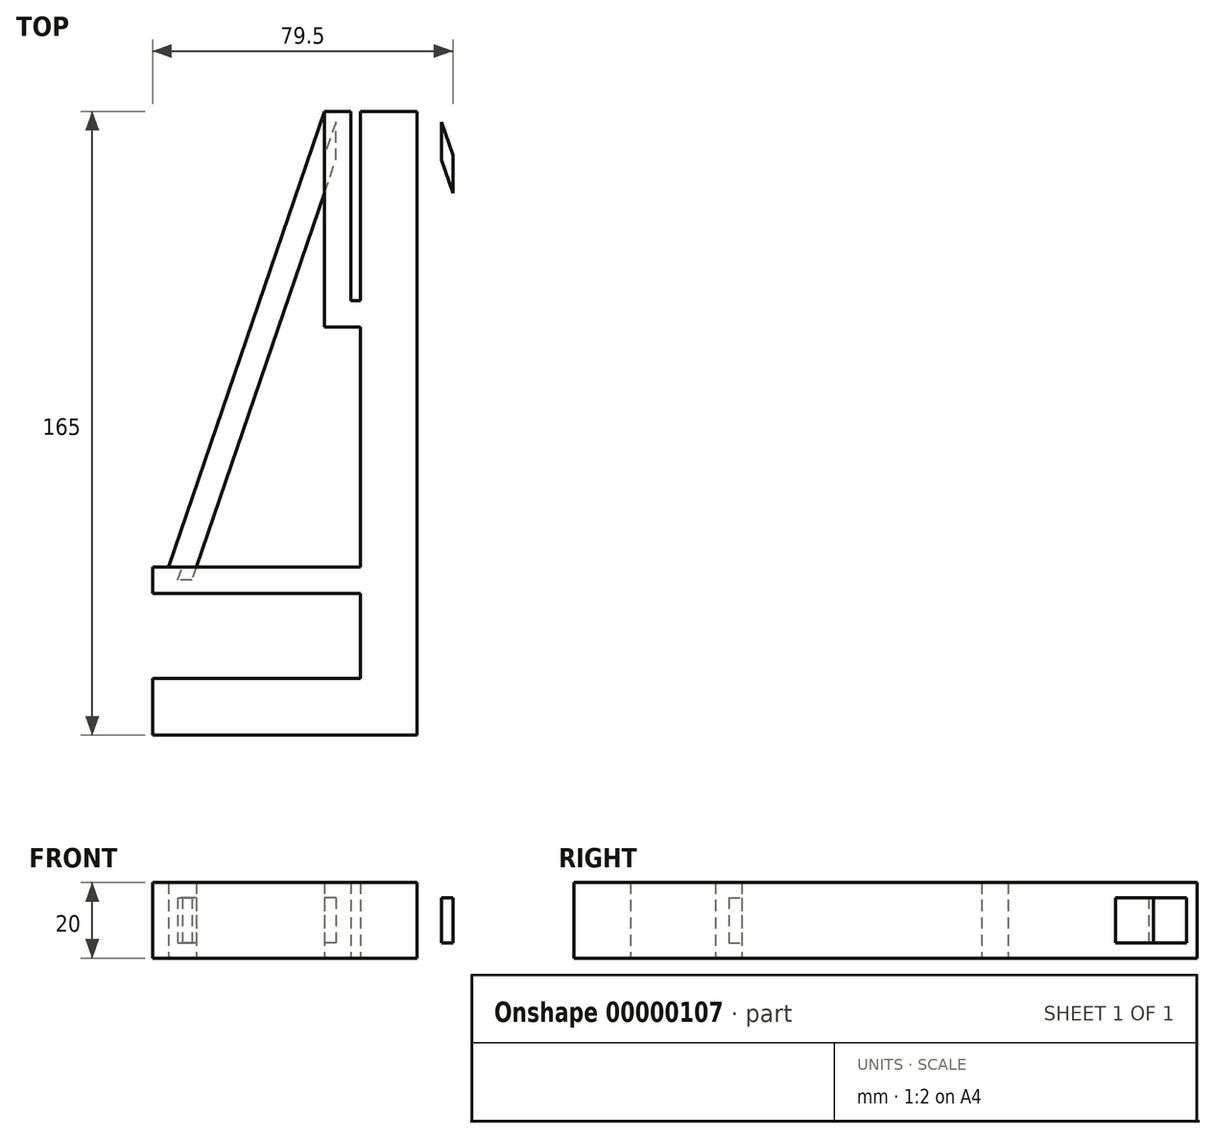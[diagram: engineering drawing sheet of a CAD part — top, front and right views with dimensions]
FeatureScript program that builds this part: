
annotation { "Feature Type Name" : "Feature", "Feature Type Description" : "" }
export const myFeature = defineFeature(function(context is Context, id is Id, definition is map)
    precondition{}
    {
        {
            var Q0;
            Q0=qCreatedBy(makeId("Top.planeOp"),FACE);
            var sketch = newSketch(context, id + "F0", { "sketchPlane" : qUnion([Q0])});
            skLineSegment(sketch, "E0.rect.bottom", {"start": v(7.5, 75) * mm, "end": v(-7.5, 75) * mm});
            skLineSegment(sketch, "E0.rect.left", {"start": v(7.5, 75) * mm, "end": v(7.5, -75) * mm});
            skLineSegment(sketch, "E0.rect.right", {"start": v(-7.5, 75) * mm, "end": v(-7.5, 25) * mm});
            skPoint(sketch, "E0.rect.middle", {"position": v(0, 0) * mm});
            skLineSegment(sketch, "E1.bottom", {"start": v(-7.5, -75) * mm, "end": v(-62.5, -75) * mm});
            skLineSegment(sketch, "E1.top", {"start": v(7.5, -90) * mm, "end": v(-62.5, -90) * mm});
            skLineSegment(sketch, "E1.left", {"start": v(7.5, -75) * mm, "end": v(7.5, -90) * mm});
            skLineSegment(sketch, "E1.right", {"start": v(-62.5, -75) * mm, "end": v(-62.5, -90) * mm});
            skLineSegment(sketch, "E2.bottom", {"start": v(-7.5, -52.5) * mm, "end": v(-62.5, -52.5) * mm});
            skLineSegment(sketch, "E2.top", {"start": v(-7.5, -45.5) * mm, "end": v(-62.5, -45.5) * mm});
            skLineSegment(sketch, "E2.right", {"start": v(-62.5, -52.5) * mm, "end": v(-62.5, -45.5) * mm});
            skLineSegment(sketch, "E3.bottom", {"start": v(-7.5, 18) * mm, "end": v(-17, 18) * mm});
            skLineSegment(sketch, "E3.top", {"start": v(-7.5, 25) * mm, "end": v(-10, 25) * mm});
            skLineSegment(sketch, "E3.right", {"start": v(-17, 18) * mm, "end": v(-17, 25) * mm});
            skLineSegment(sketch, "E4.top", {"start": v(-17, 75) * mm, "end": v(-10, 75) * mm});
            skLineSegment(sketch, "E4.left", {"start": v(-17, 25) * mm, "end": v(-17, 75) * mm});
            skLineSegment(sketch, "E4.right", {"start": v(-10, 25) * mm, "end": v(-10, 75) * mm});
            skLineSegment(sketch, "E5", {"start": v(-17, 75) * mm, "end": v(-58.31, -45.5) * mm, "construction": true});
            skLineSegment(sketch, "E6", {"start": v(-58.31, -45.5) * mm, "end": v(-50.91, -45.5) * mm});
            skLineSegment(sketch, "E7", {"start": v(-50.91, -45.5) * mm, "end": v(-17, 53.42) * mm, "construction": true});
            skLineSegment(sketch, "E8", {"start": v(-17, 53.42) * mm, "end": v(-14, 62.17) * mm, "construction": true});
            skLineSegment(sketch, "E9", {"start": v(-14, 62.17) * mm, "end": v(-14, 72.17) * mm, "construction": true});
            skLineSegment(sketch, "E10", {"start": v(-14, 72.17) * mm, "end": v(-17, 63.42) * mm, "construction": true});
            skLineSegment(sketch, "E11", {"start": v(-50.91, -45.5) * mm, "end": v(-52.11, -49) * mm});
            skLineSegment(sketch, "E12", {"start": v(-52.11, -49) * mm, "end": v(-55.81, -49) * mm});
            skLineSegment(sketch, "E13", {"start": v(-55.81, -49) * mm, "end": v(-54.61, -45.5) * mm});
            skLineSegment(sketch, "E14", {"start": v(-54.61, -45.5) * mm, "end": v(-50.91, -45.5) * mm});
            skPoint(sketch, "E15.orphan", {"position": v(7.5, -75) * mm});
            skLineSegment(sketch, "E16.trimOffspring", {"start": v(-7.5, -52.5) * mm, "end": v(-7.5, -75) * mm});
            skLineSegment(sketch, "E17.trimOffspring", {"start": v(-7.5, 18) * mm, "end": v(-7.5, -45.5) * mm});
            skSolve(sketch);
        }
        {
            var Q0;
            {var subQ3=sQuery(id+"F0.wireOp",EDGE,"E11");var subQ4=makeQuery(id+"F0.imprint","IMPRINT",EDGE,{"derivedFrom":subQ3});Q0=qUnion([makeQuery(id+"F0.imprint","IMPRINT",FACE,{"disambiguationData":[TD([[makeQuery(id+"F0.imprint","IMPRINT",EDGE,{"derivedFrom":sQuery(id+"F0.wireOp",EDGE,"E0.rect.bottom")}),1.0]])]}),makeQuery(id+"F0.imprint","IMPRINT",FACE,{"disambiguationData":[TD([[subQ4,-1.0]])]})]);}
            extrude(context, id + "F1", {"entities" : qUnion([Q0]), "depth" : 20 * mm});
        }
        {
            var Q0;
            Q0=makeQuery(id+"F0.imprint","IMPRINT",FACE,{"disambiguationData":[TD([[makeQuery(id+"F0.imprint","IMPRINT",EDGE,{"derivedFrom":sQuery(id+"F0.wireOp",EDGE,"E0.rect.bottom")}),1.0]])]});
            cPlane(context, id + "F2", {"entities" : qUnion([Q0]), "cplaneType" : CPlaneType.OFFSET, "offset" : 4 * mm, "width" : 150 * mm, "height" : 150 * mm});
        }
        {
            var Q0;
            Q0=qCreatedBy(id+"F2.planeOp",FACE);
            var sketch = newSketch(context, id + "F3", { "sketchPlane" : qUnion([Q0])});
            skLineSegment(sketch, "E18", {"start": v(-14, 72.17) * mm, "end": v(-17, 63.42) * mm});
            skLineSegment(sketch, "E19", {"start": v(-17, 63.42) * mm, "end": v(-17, 53.42) * mm});
            skLineSegment(sketch, "E20", {"start": v(-17, 53.42) * mm, "end": v(-14, 62.17) * mm});
            skLineSegment(sketch, "E21", {"start": v(-14, 62.17) * mm, "end": v(-14, 72.17) * mm});
            skLineSegment(sketch, "E22", {"start": v(-55.81, -49) * mm, "end": v(-54.61, -45.5) * mm});
            skLineSegment(sketch, "E23", {"start": v(-54.61, -45.5) * mm, "end": v(-50.91, -45.5) * mm});
            skLineSegment(sketch, "E24", {"start": v(-50.91, -45.5) * mm, "end": v(-52.11, -49) * mm});
            skLineSegment(sketch, "E25", {"start": v(-52.11, -49) * mm, "end": v(-55.81, -49) * mm});
            skSolve(sketch);
        }
        {
            var Q0;
            {Q0=qUnion([makeQuery(id+"F3.imprint","IMPRINT",FACE,{"disambiguationData":[TD([[makeQuery(id+"F3.imprint","IMPRINT",EDGE,{"derivedFrom":sQuery(id+"F3.wireOp",EDGE,"E18")}),1.0]])]}),makeQuery(id+"F3.imprint","IMPRINT",FACE,{"disambiguationData":[TD([[makeQuery(id+"F3.imprint","IMPRINT",EDGE,{"derivedFrom":sQuery(id+"F3.wireOp",EDGE,"E22")}),-1.0]])]})]);}
            extrude(context, id + "F4", {"entities" : qUnion([Q0]), "operationType" : NewBodyOperationType.REMOVE, "depth" : 12 * mm});
        }
        {
            var Q0;
            Q0=qCreatedBy(id+"F2.planeOp",FACE);
            var sketch = newSketch(context, id + "F5", { "sketchPlane" : qUnion([Q0])});
            skLineSegment(sketch, "E26", {"start": v(-14, 72.17) * mm, "end": v(-17, 63.42) * mm});
            skLineSegment(sketch, "E27", {"start": v(-17, 63.42) * mm, "end": v(-17, 53.42) * mm});
            skLineSegment(sketch, "E28", {"start": v(-17, 53.42) * mm, "end": v(-14, 62.17) * mm});
            skLineSegment(sketch, "E29", {"start": v(-14, 62.17) * mm, "end": v(-14, 72.17) * mm});
            skLineSegment(sketch, "E30", {"start": v(-54.61, -45.5) * mm, "end": v(-50.91, -45.5) * mm});
            skLineSegment(sketch, "E31", {"start": v(-50.91, -45.5) * mm, "end": v(-52.11, -49) * mm});
            skLineSegment(sketch, "E32", {"start": v(-52.11, -49) * mm, "end": v(-55.81, -49) * mm});
            skLineSegment(sketch, "E33", {"start": v(-55.81, -49) * mm, "end": v(-54.61, -45.5) * mm});
            skSolve(sketch);
        }
        {
            var Q0;
            {Q0=qUnion([makeQuery(id+"F5.imprint","IMPRINT",FACE,{"disambiguationData":[TD([[makeQuery(id+"F5.imprint","IMPRINT",EDGE,{"derivedFrom":sQuery(id+"F5.wireOp",EDGE,"E26")}),1.0]])]}),makeQuery(id+"F5.imprint","IMPRINT",FACE,{"disambiguationData":[TD([[makeQuery(id+"F5.imprint","IMPRINT",EDGE,{"derivedFrom":sQuery(id+"F5.wireOp",EDGE,"E30")}),-1.0]])]})]);}
            extrude(context, id + "F6", {"entities" : qUnion([Q0]), "depth" : 12 * mm});
        }
        {
            var Q0;
            Q0=qCreatedBy(makeId("Top.planeOp"),FACE);
            var sketch = newSketch(context, id + "F7", { "sketchPlane" : qUnion([Q0])});
            skLineSegment(sketch, "E34", {"start": v(-17, 75) * mm, "end": v(-58.31, -45.5) * mm});
            skLineSegment(sketch, "E35", {"start": v(-58.31, -45.5) * mm, "end": v(-50.91, -45.5) * mm});
            skLineSegment(sketch, "E36", {"start": v(-50.91, -45.5) * mm, "end": v(-17, 53.42) * mm});
            skLineSegment(sketch, "E37", {"start": v(-17, 53.42) * mm, "end": v(-17, 75) * mm});
            skSolve(sketch);
        }
        {
            var Q0;
            Q0=makeQuery(id+"F7.imprint","IMPRINT",FACE,{"disambiguationData":[TD([[makeQuery(id+"F7.imprint","IMPRINT",EDGE,{"derivedFrom":sQuery(id+"F7.wireOp",EDGE,"E34")}),1.0]])]});
            extrude(context, id + "F8", {"entities" : qUnion([Q0]), "depth" : 20 * mm});
        }
        {
            var Q0;
            Q0=makeQuery(id+"F6.opExtrude","SWEPT_BODY",BODY,{"disambiguationData":[OSD([sQuery(id+"F5.wireOp",EDGE,"E26"),sQuery(id+"F5.wireOp",EDGE,"E27"),sQuery(id+"F5.wireOp",EDGE,"E28"),sQuery(id+"F5.wireOp",EDGE,"E29")])]});
            var Q1;
            Q1=qCreatedBy(makeId("Right.planeOp"),FACE);
            mirror(context, id + "F9", {"entities" : qUnion([Q0]), "mirrorPlane" : qUnion([Q1])});
        }
        {
            var Q0;
            Q0=makeQuery(id+"F6.opExtrude","SWEPT_BODY",BODY,{"disambiguationData":[OSD([sQuery(id+"F5.wireOp",EDGE,"E26"),sQuery(id+"F5.wireOp",EDGE,"E27"),sQuery(id+"F5.wireOp",EDGE,"E28"),sQuery(id+"F5.wireOp",EDGE,"E29")])]});
            deleteBodies(context, id + "F10", {"entities" : qUnion([Q0])});
        }
    });
